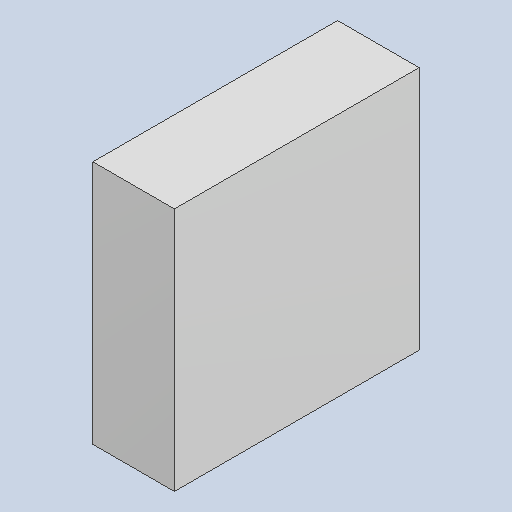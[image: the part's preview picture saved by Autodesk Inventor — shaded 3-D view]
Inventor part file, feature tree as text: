
AUTODESK INVENTOR PART (.ipt)
format: ipt  version: 2023.4 (Build 274418000, 418)  size: 81,408 bytes
history: native  units: mm
features: extrude x1
ambient origin geometry x8: Origin, YZ Plane, XZ Plane, XY Plane, X Axis, Y Axis, Z Axis, Center Point
bodies: Solid1 (feature_tree)
feature tree (1):
  extrude  "Extruded_27"  [1 undecoded]
note: 1 required parameter value undecoded (feature->parameter linkage not recoverable at this tier; creation-order binding heuristic only, values carry confidence <= 0.55)
